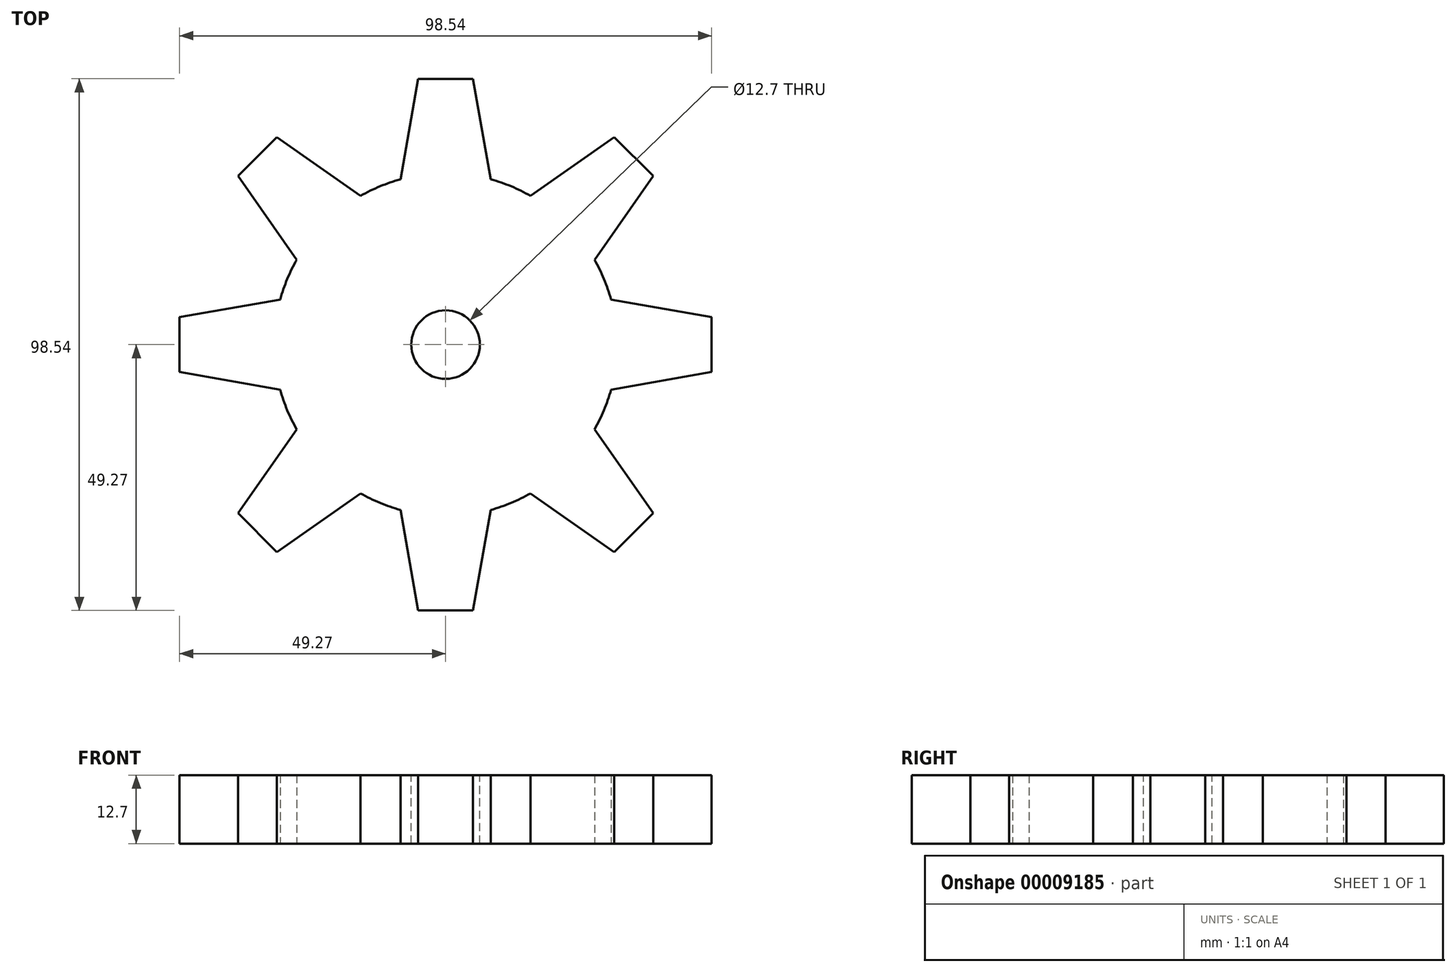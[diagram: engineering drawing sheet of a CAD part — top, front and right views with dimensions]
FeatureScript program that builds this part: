
annotation { "Feature Type Name" : "Feature", "Feature Type Description" : "" }
export const myFeature = defineFeature(function(context is Context, id is Id, definition is map)
    precondition{}
    {
        {
            var Q0;
            Q0=qCreatedBy(makeId("Top.planeOp"),FACE);
            var sketch = newSketch(context, id + "F0", { "sketchPlane" : qUnion([Q0])});
            skCircle(sketch, "E0", {"center": v(0, 0) * mm, "radius": 31.75 * mm});
            skLineSegment(sketch, "E1", {"start": v(0, 0) * mm, "end": v(0, 31.75) * mm, "construction": true});
            skLineSegment(sketch, "E2", {"start": v(-8.37, 30.63) * mm, "end": v(-5.08, 49.27) * mm});
            skLineSegment(sketch, "E3", {"start": v(-5.08, 49.27) * mm, "end": v(0, 49.27) * mm});
            skLineSegment(sketch, "E4.MirrorCS", {"start": v(8.37, 30.63) * mm, "end": v(5.08, 49.27) * mm});
            skLineSegment(sketch, "E5.MirrorCS", {"start": v(5.08, 49.27) * mm, "end": v(0, 49.27) * mm});
            skLineSegment(sketch, "E6.1.0", {"start": v(-27.57, 15.74) * mm, "end": v(-38.43, 31.25) * mm});
            skLineSegment(sketch, "E6.1.1", {"start": v(-38.43, 31.25) * mm, "end": v(-34.84, 34.84) * mm});
            skLineSegment(sketch, "E6.1.2", {"start": v(-31.25, 38.43) * mm, "end": v(-34.84, 34.84) * mm});
            skLineSegment(sketch, "E6.1.3", {"start": v(-15.74, 27.57) * mm, "end": v(-31.25, 38.43) * mm});
            skLineSegment(sketch, "E6.2.0", {"start": v(-30.63, -8.37) * mm, "end": v(-49.27, -5.08) * mm});
            skLineSegment(sketch, "E6.2.1", {"start": v(-49.27, -5.08) * mm, "end": v(-49.27, 0) * mm});
            skLineSegment(sketch, "E6.2.2", {"start": v(-49.27, 5.08) * mm, "end": v(-49.27, 0) * mm});
            skLineSegment(sketch, "E6.2.3", {"start": v(-30.63, 8.37) * mm, "end": v(-49.27, 5.08) * mm});
            skLineSegment(sketch, "E6.3.0", {"start": v(-15.74, -27.57) * mm, "end": v(-31.25, -38.43) * mm});
            skLineSegment(sketch, "E6.3.1", {"start": v(-31.25, -38.43) * mm, "end": v(-34.84, -34.84) * mm});
            skLineSegment(sketch, "E6.3.2", {"start": v(-38.43, -31.25) * mm, "end": v(-34.84, -34.84) * mm});
            skLineSegment(sketch, "E6.3.3", {"start": v(-27.57, -15.74) * mm, "end": v(-38.43, -31.25) * mm});
            skLineSegment(sketch, "E7.1.4.0", {"start": v(8.37, -30.63) * mm, "end": v(5.08, -49.27) * mm});
            skLineSegment(sketch, "E7.3.4.0", {"start": v(5.08, -49.27) * mm, "end": v(0, -49.27) * mm});
            skLineSegment(sketch, "E7.6.4.0", {"start": v(-5.08, -49.27) * mm, "end": v(0, -49.27) * mm});
            skLineSegment(sketch, "E7.9.4.0", {"start": v(-8.37, -30.63) * mm, "end": v(-5.08, -49.27) * mm});
            skLineSegment(sketch, "E7.1.5.0", {"start": v(27.57, -15.74) * mm, "end": v(38.43, -31.25) * mm});
            skLineSegment(sketch, "E7.3.5.0", {"start": v(38.43, -31.25) * mm, "end": v(34.84, -34.84) * mm});
            skLineSegment(sketch, "E7.6.5.0", {"start": v(31.25, -38.43) * mm, "end": v(34.84, -34.84) * mm});
            skLineSegment(sketch, "E7.9.5.0", {"start": v(15.74, -27.57) * mm, "end": v(31.25, -38.43) * mm});
            skLineSegment(sketch, "E7.1.6.0", {"start": v(30.63, 8.37) * mm, "end": v(49.27, 5.08) * mm});
            skLineSegment(sketch, "E7.3.6.0", {"start": v(49.27, 5.08) * mm, "end": v(49.27, 0) * mm});
            skLineSegment(sketch, "E7.6.6.0", {"start": v(49.27, -5.08) * mm, "end": v(49.27, 0) * mm});
            skLineSegment(sketch, "E7.9.6.0", {"start": v(30.63, -8.37) * mm, "end": v(49.27, -5.08) * mm});
            skLineSegment(sketch, "E8.1.7.0", {"start": v(15.74, 27.57) * mm, "end": v(31.25, 38.43) * mm});
            skLineSegment(sketch, "E8.3.7.0", {"start": v(31.25, 38.43) * mm, "end": v(34.84, 34.84) * mm});
            skLineSegment(sketch, "E8.6.7.0", {"start": v(38.43, 31.25) * mm, "end": v(34.84, 34.84) * mm});
            skLineSegment(sketch, "E8.9.7.0", {"start": v(27.57, 15.74) * mm, "end": v(38.43, 31.25) * mm});
            skSolve(sketch);
        }
        {
            var Q0;
            {var subQ0=sQuery(id+"F0.wireOp",EDGE,"E0");var subQ8=makeQuery(id+"F0.imprint","INTERSECT",VERTEX,{"derivedFrom":[subQ0,sQuery(id+"F0.wireOp",EDGE,"E7.1.6.0")]});Q0=makeQuery(id+"F0.imprint","IMPRINT",FACE,{"disambiguationData":[TD([[makeQuery(id+"F0.imprint","IMPRINT",EDGE,{"disambiguationData":[TD([[subQ8,-1.0]])],"derivedFrom":subQ0}),1.0]])]});}
            var Q1;
            {var subQ1=sQuery(id+"F0.wireOp",EDGE,"E6.1.0");Q1=makeQuery(id+"F0.imprint","IMPRINT",FACE,{"disambiguationData":[TD([[makeQuery(id+"F0.imprint","IMPRINT",EDGE,{"derivedFrom":subQ1}),-1.0]])]});}
            var Q2;
            {var subQ1=sQuery(id+"F0.wireOp",EDGE,"E6.2.0");Q2=makeQuery(id+"F0.imprint","IMPRINT",FACE,{"disambiguationData":[TD([[makeQuery(id+"F0.imprint","IMPRINT",EDGE,{"derivedFrom":subQ1}),-1.0]])]});}
            var Q3;
            {var subQ1=sQuery(id+"F0.wireOp",EDGE,"E6.3.0");Q3=makeQuery(id+"F0.imprint","IMPRINT",FACE,{"disambiguationData":[TD([[makeQuery(id+"F0.imprint","IMPRINT",EDGE,{"derivedFrom":subQ1}),-1.0]])]});}
            var Q4;
            {var subQ1=sQuery(id+"F0.wireOp",EDGE,"E7.1.4.0");Q4=makeQuery(id+"F0.imprint","IMPRINT",FACE,{"disambiguationData":[TD([[makeQuery(id+"F0.imprint","IMPRINT",EDGE,{"derivedFrom":subQ1}),-1.0]])]});}
            var Q5;
            {var subQ1=sQuery(id+"F0.wireOp",EDGE,"E7.1.5.0");Q5=makeQuery(id+"F0.imprint","IMPRINT",FACE,{"disambiguationData":[TD([[makeQuery(id+"F0.imprint","IMPRINT",EDGE,{"derivedFrom":subQ1}),-1.0]])]});}
            var Q6;
            {var subQ1=sQuery(id+"F0.wireOp",EDGE,"E7.1.6.0");Q6=makeQuery(id+"F0.imprint","IMPRINT",FACE,{"disambiguationData":[TD([[makeQuery(id+"F0.imprint","IMPRINT",EDGE,{"derivedFrom":subQ1}),-1.0]])]});}
            var Q7;
            {var subQ1=sQuery(id+"F0.wireOp",EDGE,"E8.1.7.0");Q7=makeQuery(id+"F0.imprint","IMPRINT",FACE,{"disambiguationData":[TD([[makeQuery(id+"F0.imprint","IMPRINT",EDGE,{"derivedFrom":subQ1}),-1.0]])]});}
            var Q8;
            {var subQ1=sQuery(id+"F0.wireOp",EDGE,"E2");Q8=makeQuery(id+"F0.imprint","IMPRINT",FACE,{"disambiguationData":[TD([[makeQuery(id+"F0.imprint","IMPRINT",EDGE,{"derivedFrom":subQ1}),-1.0]])]});}
            extrude(context, id + "F1", {"entities" : qUnion([Q0, Q1, Q2, Q3, Q4, Q5, Q6, Q7, Q8]), "depth" : 12.7 * mm});
        }
        {
            var Q0;
            Q0=makeQuery(id+"F1.opExtrude","CAP_FACE",FACE,{"disambiguationData":[OSD([sQuery(id+"F0.wireOp",EDGE,"E0"),sQuery(id+"F0.wireOp",EDGE,"E2"),sQuery(id+"F0.wireOp",EDGE,"E3"),sQuery(id+"F0.wireOp",EDGE,"E4.MirrorCS"),sQuery(id+"F0.wireOp",EDGE,"E5.MirrorCS"),sQuery(id+"F0.wireOp",EDGE,"E6.1.0"),sQuery(id+"F0.wireOp",EDGE,"E6.1.1"),sQuery(id+"F0.wireOp",EDGE,"E6.1.2"),sQuery(id+"F0.wireOp",EDGE,"E6.1.3"),sQuery(id+"F0.wireOp",EDGE,"E6.2.0"),sQuery(id+"F0.wireOp",EDGE,"E6.2.1"),sQuery(id+"F0.wireOp",EDGE,"E6.2.2"),sQuery(id+"F0.wireOp",EDGE,"E6.2.3"),sQuery(id+"F0.wireOp",EDGE,"E6.3.0"),sQuery(id+"F0.wireOp",EDGE,"E6.3.1"),sQuery(id+"F0.wireOp",EDGE,"E6.3.2"),sQuery(id+"F0.wireOp",EDGE,"E6.3.3"),sQuery(id+"F0.wireOp",EDGE,"E7.1.4.0"),sQuery(id+"F0.wireOp",EDGE,"E7.3.4.0"),sQuery(id+"F0.wireOp",EDGE,"E7.6.4.0"),sQuery(id+"F0.wireOp",EDGE,"E7.9.4.0"),sQuery(id+"F0.wireOp",EDGE,"E7.1.5.0"),sQuery(id+"F0.wireOp",EDGE,"E7.3.5.0"),sQuery(id+"F0.wireOp",EDGE,"E7.6.5.0"),sQuery(id+"F0.wireOp",EDGE,"E7.9.5.0"),sQuery(id+"F0.wireOp",EDGE,"E7.1.6.0"),sQuery(id+"F0.wireOp",EDGE,"E7.3.6.0"),sQuery(id+"F0.wireOp",EDGE,"E7.6.6.0"),sQuery(id+"F0.wireOp",EDGE,"E7.9.6.0"),sQuery(id+"F0.wireOp",EDGE,"E8.1.7.0"),sQuery(id+"F0.wireOp",EDGE,"E8.3.7.0"),sQuery(id+"F0.wireOp",EDGE,"E8.6.7.0"),sQuery(id+"F0.wireOp",EDGE,"E8.9.7.0")])],"isStart":false});
            var sketch = newSketch(context, id + "F2", { "sketchPlane" : qUnion([Q0])});
            skCircle(sketch, "E9", {"center": v(0, 0) * mm, "radius": 6.35 * mm});
            skSolve(sketch);
        }
        {
            var Q0;
            Q0=makeQuery(id+"F2.imprint","IMPRINT",FACE,{"disambiguationData":[TD([[makeQuery(id+"F2.imprint","IMPRINT",EDGE,{"derivedFrom":sQuery(id+"F2.wireOp",EDGE,"E9")}),1.0]])]});
            extrude(context, id + "F3", {"entities" : qUnion([Q0]), "operationType" : NewBodyOperationType.REMOVE, "endBound" : BoundingType.THROUGH_ALL, "oppositeDirection" : true, "depth" : 25.4 * mm});
        }
    });
